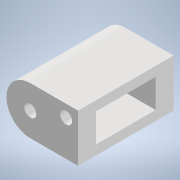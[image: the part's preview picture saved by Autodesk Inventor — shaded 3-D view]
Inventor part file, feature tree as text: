
AUTODESK INVENTOR PART (.ipt)
format: ipt  version: 2022 (Build 260153000, 153)  size: 146,944 bytes
history: native  units: mm
features: sketch x5, extrude x4, other x2, hole x1
ambient origin geometry x8: Origin, YZ Plane, XZ Plane, XY Plane, X Axis, Y Axis, Z Axis, Center Point
bodies: Solid1 (feature_tree)
feature tree (12):
  extrude  "Extrusion1"  Depth=20.0mm
  extrude  "Extrusion2"  Depth=40.0mm
  extrude  "Extrusion3"  Depth=10.0mm
  other  "Full Round Fillet1"
  other  "Full Round Fillet2"
  extrude  "Extrusion4"  Depth=25.0mm
  hole  "Hole1"  [1 undecoded]
  sketch  "Sketch1"  dims[d0=50.0mm d1=20.0mm]
  sketch  "Sketch2"  dims[d2=40.0mm d3=0.0mm d4=5.0mm]
  sketch  "Sketch3"  dims[d5=10.0mm d6=10.0mm]
  sketch  "Sketch4"  dims[d7=0.0mm d8=0.0mm d9=25.0mm]
  sketch  "Sketch5"  dims[d10=12.0mm d11=44.0mm d12=0.0mm d13=20.0mm d14=0.0mm d15=5.0mm d16=5.0mm d17=5.0mm d18=6.0mm d19=4.0mm d20=2.0mm d21=90.0deg d22=8.0mm d23=20.594885mm]
note: 1 required parameter value undecoded (feature->parameter linkage not recoverable at this tier; creation-order binding heuristic only, values carry confidence <= 0.55)
